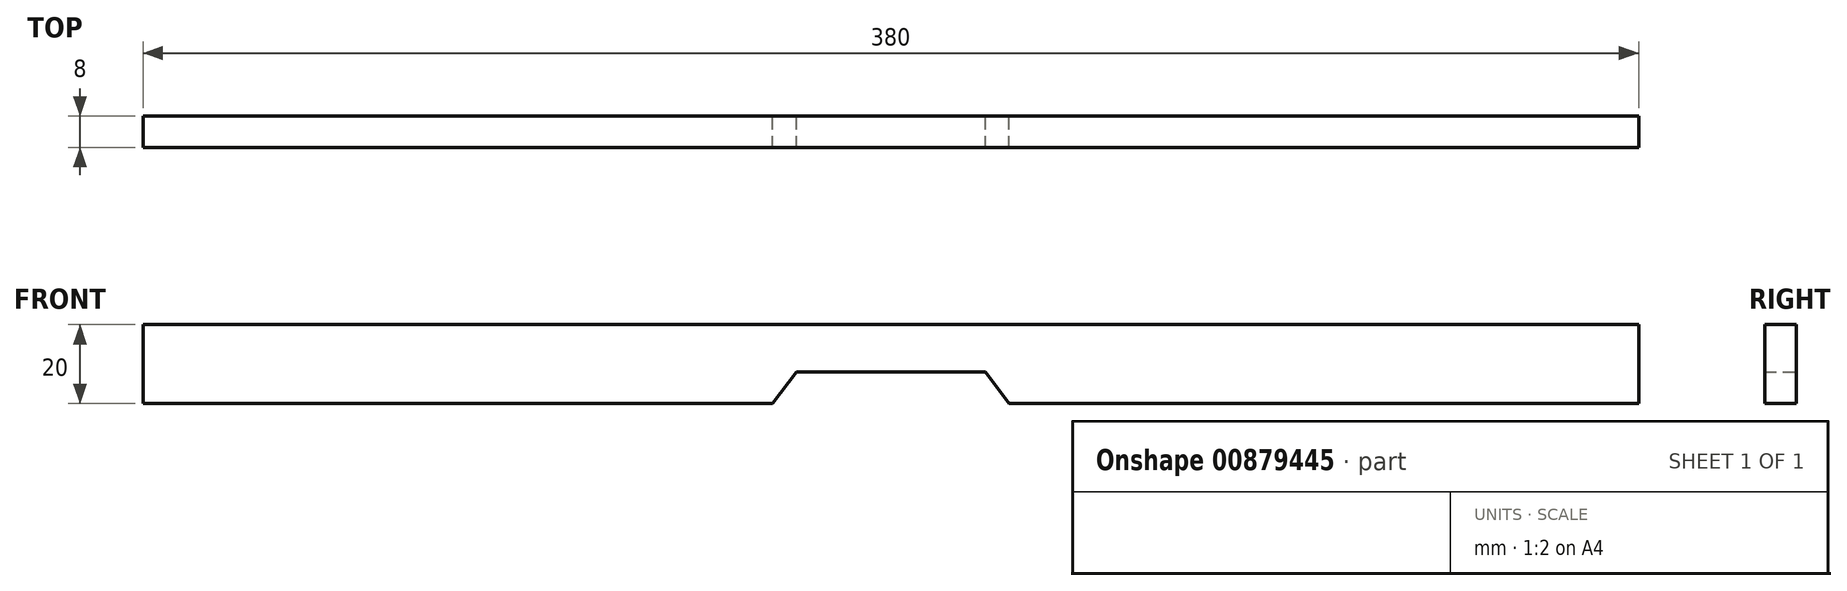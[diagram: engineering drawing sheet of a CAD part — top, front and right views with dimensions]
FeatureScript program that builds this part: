
annotation { "Feature Type Name" : "Feature", "Feature Type Description" : "" }
export const myFeature = defineFeature(function(context is Context, id is Id, definition is map)
    precondition{}
    {
        {
            var Q0;
            Q0=qCreatedBy(makeId("Front.planeOp"),FACE);
            var sketch = newSketch(context, id + "F0", { "sketchPlane" : qUnion([Q0])});
            skLineSegment(sketch, "E0.bottom", {"start": v(-190, 10) * mm, "end": v(190, 10) * mm});
            skLineSegment(sketch, "E0.top", {"start": v(-190, -10) * mm, "end": v(-30, -10) * mm});
            skLineSegment(sketch, "E0.left", {"start": v(-190, 10) * mm, "end": v(-190, -10) * mm});
            skLineSegment(sketch, "E0.right", {"start": v(190, 10) * mm, "end": v(190, -10) * mm});
            skPoint(sketch, "E0.middle", {"position": v(0, 0) * mm});
            skPoint(sketch, "E1", {"position": v(-30, -10) * mm});
            skPoint(sketch, "E2", {"position": v(30, -10) * mm});
            skPoint(sketch, "E3", {"position": v(-24, -2) * mm});
            skPoint(sketch, "E4", {"position": v(24, -2) * mm});
            skLineSegment(sketch, "E5", {"start": v(-30, -10) * mm, "end": v(-24, -2) * mm});
            skLineSegment(sketch, "E6", {"start": v(-24, -2) * mm, "end": v(24, -2) * mm});
            skLineSegment(sketch, "E7", {"start": v(24, -2) * mm, "end": v(30, -10) * mm});
            skLineSegment(sketch, "E8.trimOffspring", {"start": v(30, -10) * mm, "end": v(190, -10) * mm});
            skSolve(sketch);
        }
        {
            var Q0;
            Q0=makeQuery(id+"F0.imprint","IMPRINT",FACE,{"disambiguationData":[TD([[makeQuery(id+"F0.imprint","IMPRINT",EDGE,{"derivedFrom":sQuery(id+"F0.wireOp",EDGE,"E0.bottom")}),-1.0]])]});
            extrude(context, id + "F1", {"entities" : qUnion([Q0]), "flatOperationType" : FlatOperationType.REMOVE, "depth" : 8 * mm, "offsetDistance" : 25 * mm, "domain" : OperationDomain.MODEL});
        }
    });
